# Revit family: Bath-Shower_Trim-American_Standard- Fluent-T186.508-507
name_source: partatom
category: Plumbing Fixtures
revit_build: Autodesk Revit 2014 (Build: 20130308_1515(x64)
units: mm (PartAtom-declared; Revit-internal decimal feet)

## types (2) — shared parameters
ADA Compliant = Yes
Assembly Code = D2010700
CW Connection = Yes
CWFU = 3
Default Elevation = 0"
Diverter = Yes
Diverter_Shower Connection = 1/2"
Diverter_Shower Outlet Description = 1/2'' Global Outlet Connection
Finish = Metal-American Standard-002-Polished Chrome
Flow Rate = 1.8 gpm/6.8 L/min
HW Connection = Yes
HWFU = 3
Height = 3 7/8"
Installation Type = Wall Mounted
Length = 3 7/8"
Manufacturer = American Standard
Material = Metal-American Standard-002-Polished Chrome
Price = Prices may vary. Please consult Manufacturer Representative for most up-to-date price list.
Shower = Yes
Shower Connection Description = 1/2'' Global NPT Inlet Connection
Shower Connection Size = 1/2"
Shower Kit = Yes
Spacing from Wall = 2 5/8"
Specification = Bath/shower fitting shall feature water saving showerhead with Max. 1.8 gpm/6.8 L/min. flow rate.
URL = https://www.americanstandard-us.com
Vent Connection = No
WFU = 4
Warranty Information = Limited Lifetime Function and Finish Warranty
Waste Connection = No
Water Connection Diameter = 1/2"
Width = 1 15/16"

## per-type parameters (varying)
| type | Description | Diverter_Spout Connection | Diverter_Spout Outlet Description | Spout | Spout Connection Description | Spout Connection Size | Spout Kit |
| T186.508 | Fluent Pressure Balance Bath/Shower Trim Kit | 1/2" | 1/2'' Global Outlet Connection | Yes | 1/2'' Global Inlet Connection | 1/2" | Yes |
| T186.507 | Fluent Pressure Balance Shower Trim Kit | 0" |  | No |  | 0" | No |

note: column(s) folded — value = type name in every type: Model

## geometry (parser evidence)
native form markers: Sweep x1
no freeform markers — native parametric forms only
